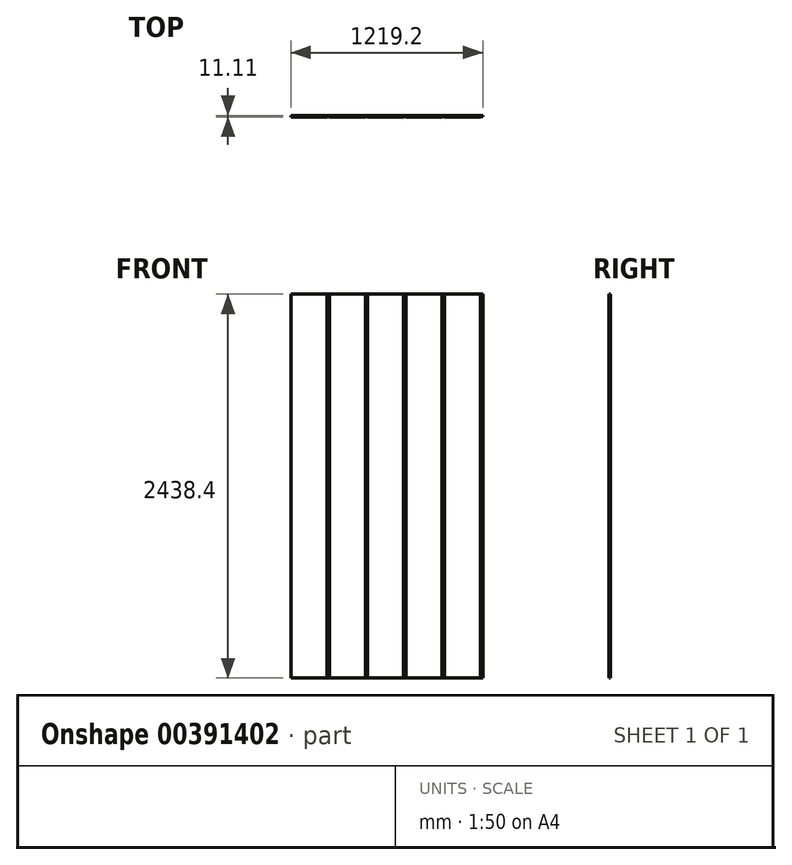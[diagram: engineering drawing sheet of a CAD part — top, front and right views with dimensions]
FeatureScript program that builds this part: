
annotation { "Feature Type Name" : "Feature", "Feature Type Description" : "" }
export const myFeature = defineFeature(function(context is Context, id is Id, definition is map)
    precondition{}
    {
        {
            var Q0;
            Q0=qCreatedBy(makeId("Front.planeOp"),FACE);
            var sketch = newSketch(context, id + "F0", { "sketchPlane" : qUnion([Q0])});
            skLineSegment(sketch, "E0.bottom", {"start": v(0, 0) * mm, "end": v(1219.2, 0) * mm});
            skLineSegment(sketch, "E0.top", {"start": v(0, 2438.4) * mm, "end": v(1219.2, 2438.4) * mm});
            skLineSegment(sketch, "E0.left", {"start": v(0, 0) * mm, "end": v(0, 2438.4) * mm});
            skLineSegment(sketch, "E0.right", {"start": v(1219.2, 0) * mm, "end": v(1219.2, 2438.4) * mm});
            skSolve(sketch);
        }
        {
            var Q0;
            Q0 = qSketchRegion(id + "F0", true);
            extrude(context, id + "F1", {"entities" : qUnion([Q0]), "depth" : 11.1 * mm});
        }
        {
            var Q0;
            Q0=makeQuery(id+"F1.opExtrude","SWEPT_FACE",FACE,{"disambiguationData":[OSD([sQuery(id+"F0.wireOp",EDGE,"E0.bottom")])]});
            var sketch = newSketch(context, id + "F2", { "sketchPlane" : qUnion([Q0])});
            skLineSegment(sketch, "E1", {"start": v(0, 11.11) * mm, "end": v(228.6, 11.11) * mm});
            skLineSegment(sketch, "E2", {"start": v(228.6, 11.11) * mm, "end": v(228.6, 6.35) * mm});
            skLineSegment(sketch, "E3", {"start": v(228.6, 6.35) * mm, "end": v(243.84, 6.35) * mm});
            skLineSegment(sketch, "E4", {"start": v(243.84, 6.35) * mm, "end": v(243.84, 11.11) * mm});
            skLineSegment(sketch, "E5", {"start": v(243.84, 11.11) * mm, "end": v(472.44, 11.11) * mm});
            skLineSegment(sketch, "E6", {"start": v(472.44, 11.11) * mm, "end": v(472.44, 6.35) * mm});
            skLineSegment(sketch, "E7", {"start": v(472.44, 6.35) * mm, "end": v(487.68, 6.35) * mm});
            skLineSegment(sketch, "E8", {"start": v(487.68, 6.35) * mm, "end": v(487.68, 11.11) * mm});
            skLineSegment(sketch, "E9", {"start": v(487.68, 11.11) * mm, "end": v(716.28, 11.11) * mm});
            skLineSegment(sketch, "E10.1.0.0", {"start": v(731.52, 11.11) * mm, "end": v(960.12, 11.11) * mm});
            skLineSegment(sketch, "E10.1.0.1", {"start": v(731.52, 6.35) * mm, "end": v(731.52, 11.11) * mm});
            skLineSegment(sketch, "E10.1.0.2", {"start": v(716.28, 6.35) * mm, "end": v(731.52, 6.35) * mm});
            skLineSegment(sketch, "E10.1.0.3", {"start": v(716.28, 11.11) * mm, "end": v(716.28, 6.35) * mm});
            skLineSegment(sketch, "E10.2.0.0", {"start": v(975.36, 11.11) * mm, "end": v(1203.96, 11.11) * mm});
            skLineSegment(sketch, "E10.2.0.1", {"start": v(975.36, 6.35) * mm, "end": v(975.36, 11.11) * mm});
            skLineSegment(sketch, "E10.2.0.2", {"start": v(960.12, 6.35) * mm, "end": v(975.36, 6.35) * mm});
            skLineSegment(sketch, "E10.2.0.3", {"start": v(960.12, 11.11) * mm, "end": v(960.12, 6.35) * mm});
            skLineSegment(sketch, "E10.direction1", {"start": v(472.44, 6.35) * mm, "end": v(716.28, 6.35) * mm, "construction": true});
            skLineSegment(sketch, "E11", {"start": v(1203.96, 11.11) * mm, "end": v(1203.96, 6.35) * mm});
            skLineSegment(sketch, "E12", {"start": v(1203.96, 6.35) * mm, "end": v(1219.2, 6.35) * mm});
            skLineSegment(sketch, "E13", {"start": v(1219.2, 6.35) * mm, "end": v(1219.2, 25.3) * mm});
            skLineSegment(sketch, "E14", {"start": v(1219.2, 25.3) * mm, "end": v(0, 32.13) * mm});
            skLineSegment(sketch, "E15", {"start": v(0, 32.13) * mm, "end": v(0, 11.11) * mm});
            skSolve(sketch);
        }
        {
            var Q0;
            Q0 = qSketchRegion(id + "F2", true);
            extrude(context, id + "F3", {"entities" : qUnion([Q0]), "operationType" : NewBodyOperationType.REMOVE, "oppositeDirection" : true, "depth" : 2540 * mm});
        }
    });
